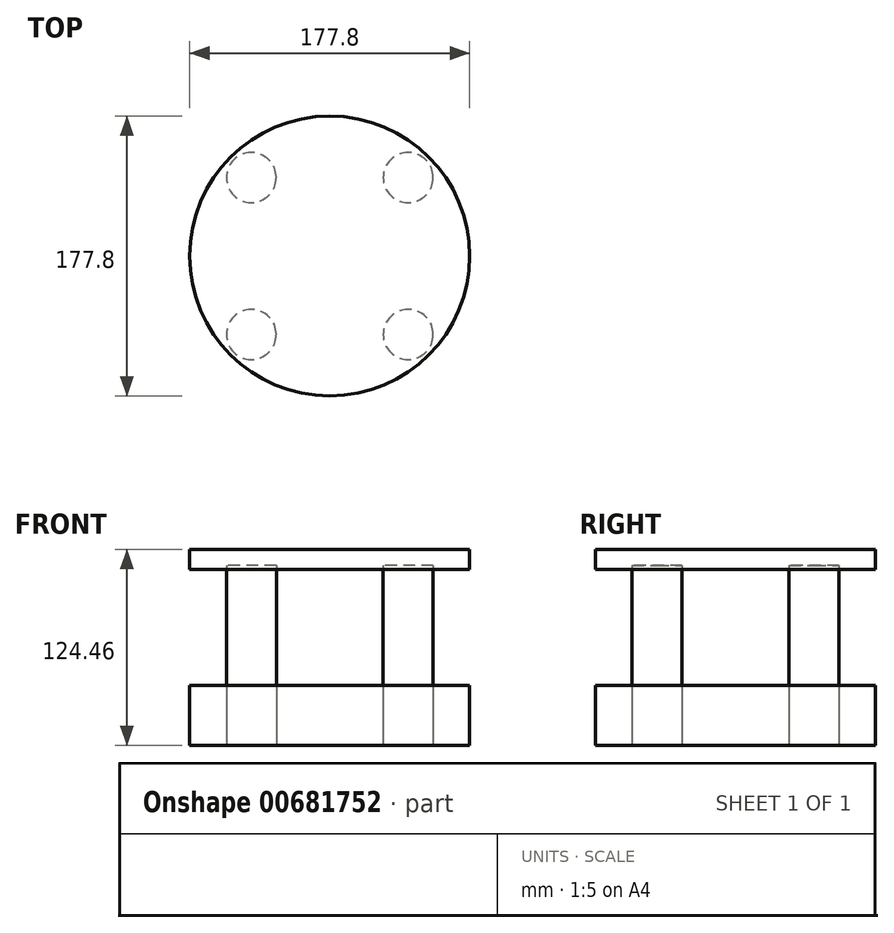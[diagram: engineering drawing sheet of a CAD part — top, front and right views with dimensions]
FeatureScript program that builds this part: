
annotation { "Feature Type Name" : "Feature", "Feature Type Description" : "" }
export const myFeature = defineFeature(function(context is Context, id is Id, definition is map)
    precondition{}
    {
        {
            var Q0;
            Q0=qCreatedBy(makeId("Top.planeOp"),FACE);
            var sketch = newSketch(context, id + "F0", { "sketchPlane" : qUnion([Q0])});
            skCircle(sketch, "E0", {"center": v(0, 0) * mm, "radius": 88.9 * mm});
            skSolve(sketch);
        }
        {
            var Q0;
            Q0 = qSketchRegion(id + "F0", true);
            extrude(context, id + "F1", {"entities" : qUnion([Q0]), "depth" : 38.1 * mm, "offsetDistance" : 25.4 * mm});
        }
        {
            var Q0;
            Q0=qCreatedBy(makeId("Top.planeOp"),FACE);
            var sketch = newSketch(context, id + "F2", { "sketchPlane" : qUnion([Q0])});
            skCircle(sketch, "E1", {"center": v(-49.84, 49.84) * mm, "radius": 15.88 * mm});
            skCircle(sketch, "E2.MirrorC", {"center": v(49.84, 49.84) * mm, "radius": 15.88 * mm});
            skCircle(sketch, "E3.MirrorC", {"center": v(-49.84, -49.84) * mm, "radius": 15.88 * mm});
            skCircle(sketch, "E4.MirrorC", {"center": v(49.84, -49.84) * mm, "radius": 15.88 * mm});
            skSolve(sketch);
        }
        {
            var Q0;
            Q0 = qSketchRegion(id + "F2", true);
            extrude(context, id + "F3", {"entities" : qUnion([Q0]), "depth" : 114.3 * mm, "offsetDistance" : 25.4 * mm});
        }
        {
            var Q0;
            Q0=qCreatedBy(makeId("Top.planeOp"),FACE);
            var sketch = newSketch(context, id + "F4", { "sketchPlane" : qUnion([Q0])});
            skCircle(sketch, "E5", {"center": v(0, 0) * mm, "radius": 88.9 * mm});
            skSolve(sketch);
        }
        {
            var Q0;
            Q0 = qSketchRegion(id + "F4", true);
            extrude(context, id + "F5", {"entities" : qUnion([Q0]), "depth" : 12.7 * mm, "offsetDistance" : 25.4 * mm});
        }
        {
            var Q0;
            Q0=makeQuery(id+"F5.opExtrude","SWEPT_BODY",BODY,{"disambiguationData":[OSD([sQuery(id+"F4.wireOp",EDGE,"E5")])]});
            transform(context, id + "F6", {"entities" : qUnion([Q0]), "transformType" : TransformType.TRANSLATION_3D, "dx" : 0 * mm, "dy" : 0 * mm, "dz" : 111.76 * mm, "makeCopy" : false});
        }
    });
